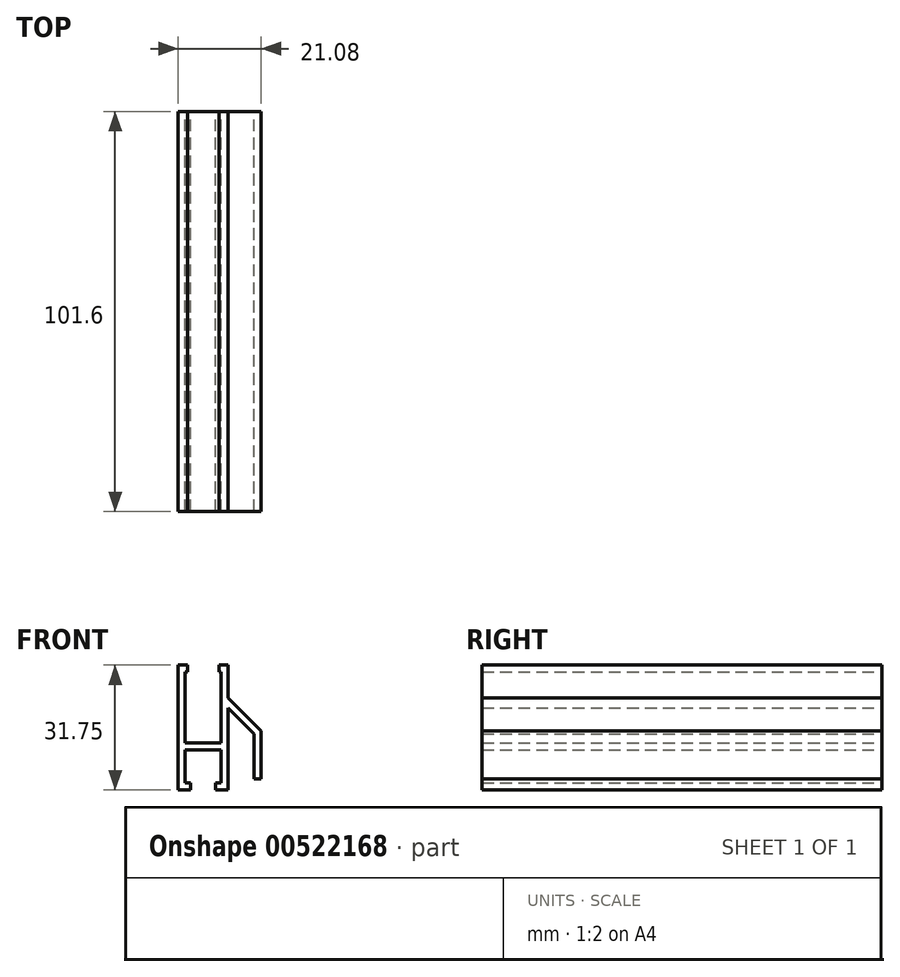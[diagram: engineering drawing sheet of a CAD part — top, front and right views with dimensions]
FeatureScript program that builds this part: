
annotation { "Feature Type Name" : "Feature", "Feature Type Description" : "" }
export const myFeature = defineFeature(function(context is Context, id is Id, definition is map)
    precondition{}
    {
        {
            var Q0;
            Q0=qCreatedBy(makeId("Front.planeOp"),FACE);
            var sketch = newSketch(context, id + "F0", { "sketchPlane" : qUnion([Q0])});
            skLineSegment(sketch, "E0", {"start": v(-4.01, 31.75) * mm, "end": v(-6.35, 31.75) * mm});
            skLineSegment(sketch, "E1", {"start": v(-6.35, 31.75) * mm, "end": v(-6.35, 0) * mm});
            skLineSegment(sketch, "E2", {"start": v(-4.57, 1.78) * mm, "end": v(-4.57, 10.16) * mm});
            skLineSegment(sketch, "E3", {"start": v(-4.57, 10.16) * mm, "end": v(4.57, 10.16) * mm});
            skLineSegment(sketch, "E4", {"start": v(4.57, 10.16) * mm, "end": v(4.57, 1.78) * mm});
            skLineSegment(sketch, "E5", {"start": v(3.17, 0) * mm, "end": v(6.35, 0) * mm});
            skLineSegment(sketch, "E6", {"start": v(6.35, 0) * mm, "end": v(6.35, 20.85) * mm});
            skLineSegment(sketch, "E7", {"start": v(6.35, 20.85) * mm, "end": v(12.95, 14.25) * mm});
            skLineSegment(sketch, "E8", {"start": v(12.95, 14.25) * mm, "end": v(12.95, 2.8) * mm});
            skLineSegment(sketch, "E9", {"start": v(12.95, 2.8) * mm, "end": v(14.73, 2.8) * mm});
            skLineSegment(sketch, "E10", {"start": v(14.73, 2.8) * mm, "end": v(14.73, 14.99) * mm});
            skLineSegment(sketch, "E11", {"start": v(14.73, 14.99) * mm, "end": v(6.35, 23.37) * mm});
            skLineSegment(sketch, "E12", {"start": v(6.35, 23.37) * mm, "end": v(6.35, 31.75) * mm});
            skLineSegment(sketch, "E13", {"start": v(6.35, 31.75) * mm, "end": v(4.01, 31.75) * mm});
            skLineSegment(sketch, "E14", {"start": v(4.01, 31.75) * mm, "end": v(4.01, 29.97) * mm});
            skLineSegment(sketch, "E15", {"start": v(4.01, 29.97) * mm, "end": v(4.57, 29.97) * mm});
            skLineSegment(sketch, "E16", {"start": v(4.57, 29.97) * mm, "end": v(4.57, 11.94) * mm});
            skLineSegment(sketch, "E17", {"start": v(4.57, 11.94) * mm, "end": v(-4.57, 11.94) * mm});
            skLineSegment(sketch, "E18", {"start": v(-4.57, 11.94) * mm, "end": v(-4.57, 29.97) * mm});
            skLineSegment(sketch, "E19", {"start": v(-4.57, 29.97) * mm, "end": v(-4.01, 29.97) * mm});
            skLineSegment(sketch, "E20", {"start": v(-4.01, 29.97) * mm, "end": v(-4.01, 31.75) * mm});
            skLineSegment(sketch, "E21", {"start": v(-4.57, 1.78) * mm, "end": v(-3.17, 1.78) * mm});
            skLineSegment(sketch, "E22", {"start": v(-3.17, 1.78) * mm, "end": v(-3.17, 0) * mm});
            skLineSegment(sketch, "E23", {"start": v(-3.17, 0) * mm, "end": v(-6.35, 0) * mm});
            skLineSegment(sketch, "E24", {"start": v(3.17, 0) * mm, "end": v(3.17, 1.78) * mm});
            skLineSegment(sketch, "E25", {"start": v(3.17, 1.78) * mm, "end": v(4.57, 1.78) * mm});
            skSolve(sketch);
        }
        {
            var Q0;
            Q0 = qSketchRegion(id + "F0", true);
            extrude(context, id + "F1", {"entities" : qUnion([Q0]), "depth" : 101.6 * mm, "offsetDistance" : 25.4 * mm});
        }
    });
